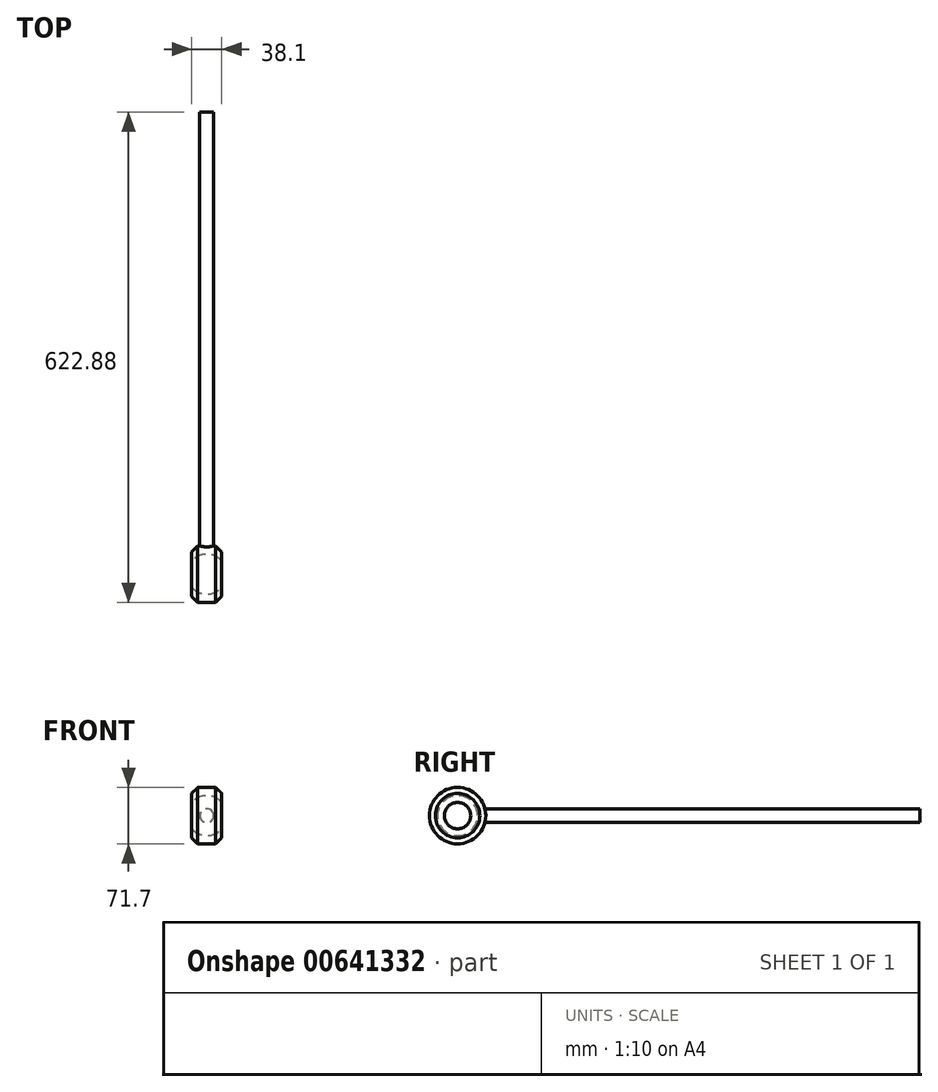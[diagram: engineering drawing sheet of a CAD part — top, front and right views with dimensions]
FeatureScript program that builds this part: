
annotation { "Feature Type Name" : "Feature", "Feature Type Description" : "" }
export const myFeature = defineFeature(function(context is Context, id is Id, definition is map)
    precondition{}
    {
        {
            var Q0;
            Q0=qCreatedBy(makeId("Right.planeOp"),FACE);
            var sketch = newSketch(context, id + "F0", { "sketchPlane" : qUnion([Q0])});
            skLineSegment(sketch, "E0", {"start": v(0, 0) * mm, "end": v(0, 19.05) * mm});
            skLineSegment(sketch, "E1", {"start": v(0, 0) * mm, "end": v(0, -19.05) * mm});
            skLineSegment(sketch, "E2", {"start": v(0, -19.05) * mm, "end": v(-19.05, -19.05) * mm});
            skLineSegment(sketch, "E3", {"start": v(0, 19.05) * mm, "end": v(-19.05, 19.05) * mm});
            skArc(sketch, "E4", {"start": v(-19.05, -19.05) * mm, "mid": v(-10.45, 0) * mm, "end": v(-19.05, 19.05) * mm});
            skLineSegment(sketch, "E5", {"start": v(-35.85, 0) * mm, "end": v(-35.85, 24.24) * mm});
            skSolve(sketch);
        }
        {
            var Q0;
            Q0=makeQuery(id+"F0.imprint","IMPRINT",FACE,{"disambiguationData":[TD([[makeQuery(id+"F0.imprint","IMPRINT",EDGE,{"derivedFrom":sQuery(id+"F0.wireOp",EDGE,"E0")}),1.0]])]});
            var Q1;
            Q1=sQuery(id+"F0.wireOp",EDGE,"E5");
            revolve(context, id + "F1", {"surfaceOperationType" : NewSurfaceOperationType.NEW, "entities" : qUnion([Q0]), "axis" : qUnion([Q1]), "revolveType" : RevolveType.FULL});
        }
        {
            var Q0;
            Q0=qCreatedBy(makeId("Front.planeOp"),FACE);
            cPlane(context, id + "F2", {"entities" : qUnion([Q0]), "cplaneType" : CPlaneType.OFFSET, "offset" : 7.62 * mm, "width" : 152.4 * mm, "height" : 152.4 * mm});
        }
        {
            var Q0;
            Q0=qCreatedBy(id+"F2.planeOp",FACE);
            var sketch = newSketch(context, id + "F3", { "sketchPlane" : qUnion([Q0])});
            skCircle(sketch, "E6", {"center": v(0, 0) * mm, "radius": 8.83 * mm});
            skSolve(sketch);
        }
        {
            var Q0;
            Q0=makeQuery(id+"F3.imprint","IMPRINT",FACE,{"disambiguationData":[TD([[makeQuery(id+"F3.imprint","IMPRINT",EDGE,{"derivedFrom":sQuery(id+"F3.wireOp",EDGE,"E6")}),1.0]])]});
            var Q1;
            Q1=sQuery(id+"F3.wireOp",EDGE,"E6");
            extrude(context, id + "F4", {"entities" : qUnion([Q0]), "operationType" : NewBodyOperationType.ADD, "surfaceOperationType" : NewSurfaceOperationType.ADD, "surfaceEntities" : qUnion([Q1]), "oppositeDirection" : true, "depth" : 558.8 * mm, "offsetDistance" : 25.4 * mm});
        }
        {
            var Q0;
            Q0=makeQuery(id+"F1.opRevolve","SWEPT_EDGE",EDGE,{"disambiguationData":[OSD([sQuery(id+"F0.wireOp",EDGE,"E0"),sQuery(id+"F0.wireOp",EDGE,"E3")])]});
            var Q1;
            Q1=makeQuery(id+"F1.opRevolve","SWEPT_EDGE",EDGE,{"disambiguationData":[OSD([sQuery(id+"F0.wireOp",EDGE,"E1"),sQuery(id+"F0.wireOp",EDGE,"E2")])]});
            chamfer(context, id + "F5", {"entities" : qUnion([Q0, Q1]), "width" : 7.62 * mm, "tangentPropagation" : true});
        }
        {
            var Q0;
            Q0=makeQuery(id+"F1.opRevolve","SWEPT_BODY",BODY,{"disambiguationData":[OSD([sQuery(id+"F0.wireOp",EDGE,"E0"),sQuery(id+"F0.wireOp",EDGE,"E1"),sQuery(id+"F0.wireOp",EDGE,"E2"),sQuery(id+"F0.wireOp",EDGE,"E3"),sQuery(id+"F0.wireOp",EDGE,"E4")])]});
            var Q1;
            Q1=makeQuery(id+"F4.opExtrude","SWEPT_FACE",FACE,{"disambiguationData":[OSD([sQuery(id+"F3.wireOp",EDGE,"E6")])]});
            transform(context, id + "F6", {"entities" : qUnion([Q0]), "transformType" : TransformType.ROTATION, "transformAxis" : qUnion([Q1]), "angle" : 90 * degree, "makeCopy" : false});
        }
    });
